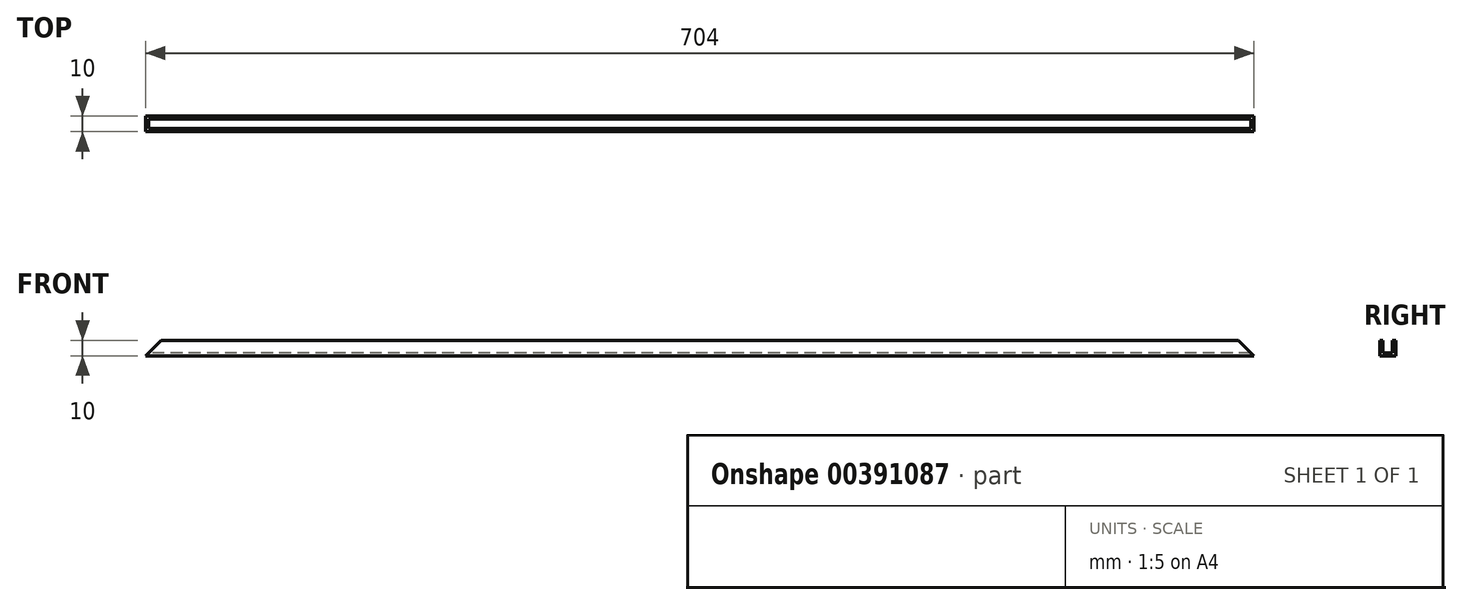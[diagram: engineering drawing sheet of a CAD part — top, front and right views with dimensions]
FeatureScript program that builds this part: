
annotation { "Feature Type Name" : "Feature", "Feature Type Description" : "" }
export const myFeature = defineFeature(function(context is Context, id is Id, definition is map)
    precondition{}
    {
        {
            var Q0;
            Q0=qCreatedBy(makeId("Right.planeOp"),FACE);
            var sketch = newSketch(context, id + "F0", { "sketchPlane" : qUnion([Q0])});
            skLineSegment(sketch, "E0.bottom", {"start": v(-5, 5) * mm, "end": v(5, 5) * mm});
            skLineSegment(sketch, "E0.top", {"start": v(-5, -5) * mm, "end": v(5, -5) * mm});
            skLineSegment(sketch, "E0.left", {"start": v(-5, 5) * mm, "end": v(-5, -5) * mm});
            skLineSegment(sketch, "E0.right", {"start": v(5, 5) * mm, "end": v(5, -5) * mm});
            skPoint(sketch, "E0.middle", {"position": v(0, 0) * mm});
            skLineSegment(sketch, "E1.bottom", {"start": v(-3, 3) * mm, "end": v(3, 3) * mm, "construction": true});
            skLineSegment(sketch, "E1.top", {"start": v(-3, -3) * mm, "end": v(3, -3) * mm, "construction": true});
            skLineSegment(sketch, "E1.left", {"start": v(-3, 3) * mm, "end": v(-3, -3) * mm, "construction": true});
            skLineSegment(sketch, "E1.right", {"start": v(3, 3) * mm, "end": v(3, -3) * mm, "construction": true});
            skLineSegment(sketch, "E2", {"start": v(-3, -3) * mm, "end": v(-3, 5) * mm});
            skLineSegment(sketch, "E3", {"start": v(-3, -3) * mm, "end": v(3, -3) * mm});
            skLineSegment(sketch, "E4", {"start": v(3, -3) * mm, "end": v(3, 5) * mm});
            skSolve(sketch);
        }
        {
            var Q0;
            Q0=makeQuery(id+"F0.imprint","IMPRINT",FACE,{"disambiguationData":[TD([[makeQuery(id+"F0.imprint","IMPRINT",EDGE,{"derivedFrom":sQuery(id+"F0.wireOp",EDGE,"E0.top")}),1.0]])]});
            extrude(context, id + "F1", {"entities" : qUnion([Q0]), "depth" : 704 * mm});
        }
        {
            var Q0;
            {var subQ0=sQuery(id+"F0.wireOp",EDGE,"E0.bottom");Q0=makeQuery(id+"F1.opExtrude","CAP_EDGE",EDGE,{"disambiguationData":[OSD([subQ0]),TDD([makeQuery(id+"F0.imprint","IMPRINT",EDGE,{"disambiguationData":[TD([[makeQuery(id+"F0.imprint","INTERSECT",VERTEX,{"derivedFrom":[subQ0,sQuery(id+"F0.wireOp",EDGE,"E0.right")]}),1.0]])],"derivedFrom":subQ0})])],"isStart":true});}
            var Q1;
            {var subQ0=sQuery(id+"F0.wireOp",EDGE,"E0.bottom");Q1=makeQuery(id+"F1.opExtrude","CAP_EDGE",EDGE,{"disambiguationData":[OSD([subQ0]),TDD([makeQuery(id+"F0.imprint","IMPRINT",EDGE,{"disambiguationData":[TD([[makeQuery(id+"F0.imprint","INTERSECT",VERTEX,{"derivedFrom":[subQ0,sQuery(id+"F0.wireOp",EDGE,"E0.left")]}),-1.0]])],"derivedFrom":subQ0})])],"isStart":true});}
            var Q2;
            {var subQ0=sQuery(id+"F0.wireOp",EDGE,"E0.bottom");Q2=makeQuery(id+"F1.opExtrude","CAP_EDGE",EDGE,{"disambiguationData":[OSD([subQ0]),TDD([makeQuery(id+"F0.imprint","IMPRINT",EDGE,{"disambiguationData":[TD([[makeQuery(id+"F0.imprint","INTERSECT",VERTEX,{"derivedFrom":[subQ0,sQuery(id+"F0.wireOp",EDGE,"E0.left")]}),-1.0]])],"derivedFrom":subQ0})])],"isStart":false});}
            chamfer(context, id + "F2", {"entities" : qUnion([Q0, Q1, Q2]), "width" : 10 * mm, "tangentPropagation" : true});
        }
    });
